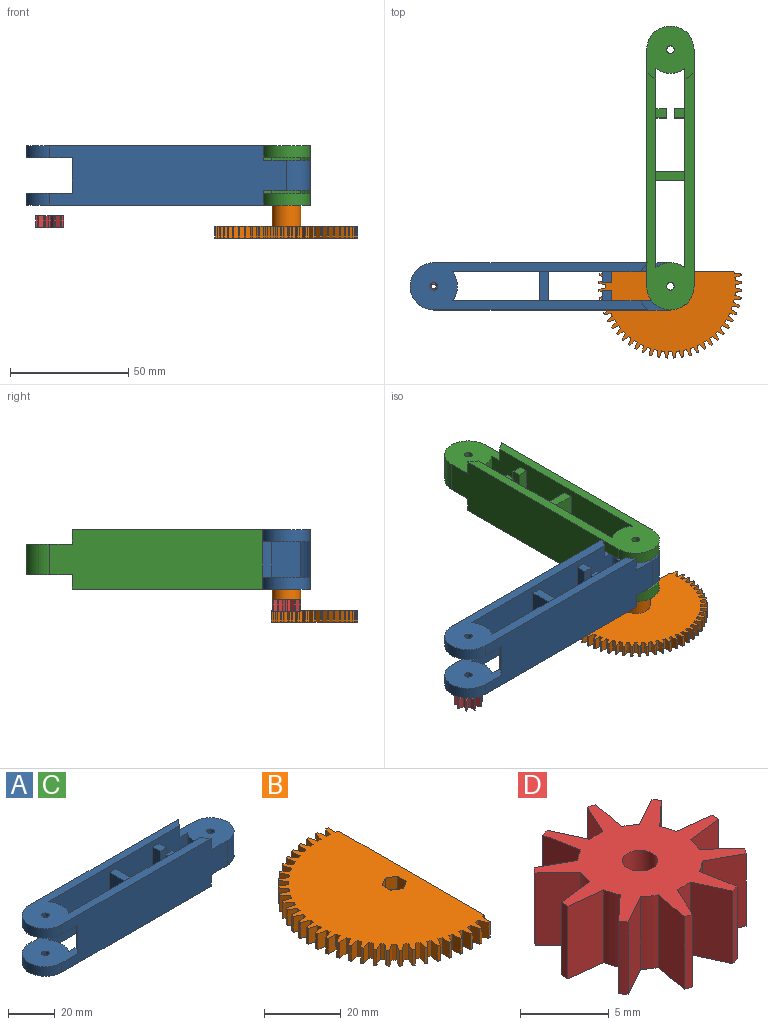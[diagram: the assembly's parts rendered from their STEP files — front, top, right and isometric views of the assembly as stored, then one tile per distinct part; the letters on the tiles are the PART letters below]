
ASSEMBLY  parts=4 mates=3
PART A: 44 faces, bbox 120x20x25 mm
  f0: plane 4.51x3.85mm, normal (0,0,1), area 17.4mm2, adj f1,f2,f5,f42
  f1: plane 19x4.51mm, normal (1,0,0), area 85.7mm2, adj f0,f3,f5,f42
  f2: plane 19x4.51mm, normal (-1,0,0), area 85.7mm2, adj f0,f3,f5,f42
  f3: plane 4.51x3.85mm, normal (0,0,-1), area 17.4mm2, adj f1,f2,f5,f42
  f4: cylinder r=1.6mm len=3.2mm, axis (0,0,-1), area 25.1mm2, adj f36,f41
  f5: plane 84.23x25mm, normal (0,1,0), area 1837.3mm2, adj f0,f1,f2,f3,f9,f11,f14,f15
  f6: plane 100x25mm, normal (0,1,0), area 2241.3mm2, adj f10,f12,f14,f20,f22,f27,f29,f30
  f7: plane 84.23x25mm, normal (0,-1,0), area 1837.3mm2, adj f9,f11,f14,f15,f16,f17,f18,f19
  f8: plane 100x25mm, normal (0,-1,0), area 2241.3mm2, adj f10,f12,f14,f20,f22,f28,f29,f31
  f9: cylinder r=10mm len=12.3mm, axis (0,0,-1), area 66.2mm2, adj f5,f7,f14,f36
  f10: cylinder r=10mm len=20mm, axis (0,0,-1), area 157.1mm2, adj f6,f8,f14,f36
  f11: cylinder r=10mm len=13mm, axis (0,0,-1), area 172.2mm2, adj f5,f7,f29,f32
  f12: cylinder r=10mm len=20mm, axis (0,0,-1), area 408.4mm2, adj f6,f8,f29,f32
  f13: cylinder r=1.6mm len=13mm, axis (0,0,-1), area 130.7mm2, adj f29,f32
  f14: plane 100.42x20mm, normal (0,0,-1), area 905.8mm2, adj f5,f6,f7,f8,f9,f10,f30,f31
  f15: plane 19x12.3mm, normal (-1,0,0), area 233.7mm2, adj f5,f7,f24,f25
  f16: plane 19x4.51mm, normal (1,0,0), area 85.7mm2, adj f7,f23,f26,f43
  f17: plane 19x12.3mm, normal (1,0,0), area 233.7mm2, adj f5,f7,f24,f25
  f18: plane 19x4.51mm, normal (-1,0,0), area 85.7mm2, adj f7,f23,f26,f43
  f19: cylinder r=10mm len=12.3mm, axis (0,0,-1), area 66.2mm2, adj f5,f7,f22,f35
  f20: cylinder r=10mm len=20mm, axis (0,0,-1), area 157.1mm2, adj f6,f8,f22,f35
  f21: cylinder r=1.6mm len=5mm, axis (0,0,-1), area 50.3mm2, adj f22,f35
  f22: plane 100.42x20mm, normal (0,0,1), area 947.8mm2, adj f5,f6,f7,f8,f19,f20,f21,f27
  f23: plane 4.51x3.85mm, normal (0,0,1), area 17.4mm2, adj f7,f16,f18,f43
  f24: plane 12.3x3.85mm, normal (0,0,1), area 47.4mm2, adj f5,f7,f15,f17
  f25: plane 12.3x3.85mm, normal (0,0,-1), area 47.4mm2, adj f5,f7,f15,f17
  f26: plane 4.51x3.85mm, normal (0,0,-1), area 17.4mm2, adj f7,f16,f18,f43
  f27: cylinder r=13.85mm len=6mm, axis (0,0,-1), area 28.8mm2, adj f6,f7,f22,f29
  f28: cylinder r=13.85mm len=6mm, axis (0,0,-1), area 28.8mm2, adj f5,f8,f22,f29
  f29: plane 22.41x20mm, normal (0,0,1), area 349.8mm2, adj f5,f6,f7,f8,f11,f12,f13,f27
  f30: cylinder r=13.85mm len=6mm, axis (0,0,-1), area 28.8mm2, adj f6,f7,f14,f32
  f31: cylinder r=13.85mm len=6mm, axis (0,0,-1), area 28.8mm2, adj f5,f8,f14,f32
  f32: plane 22.41x20mm, normal (0,0,-1), area 349.8mm2, adj f5,f6,f7,f8,f11,f12,f13,f30
  f33: cylinder r=13.85mm len=15mm, axis (0,0,-1), area 72mm2, adj f6,f7,f35,f36
  f34: cylinder r=13.85mm len=15mm, axis (0,0,-1), area 72mm2, adj f5,f8,f35,f36
  f35: plane 22.41x20mm, normal (0,0,-1), area 349.8mm2, adj f5,f6,f7,f8,f19,f20,f21,f33
  f36: plane 22.41x20mm, normal (0,0,1), area 349.8mm2, adj f4,f5,f6,f7,f8,f9,f10,f33
  f37: plane 5x2.5mm, normal (0,1,0), area 12.5mm2, adj f14,f38,f40,f41
  f38: plane 10x2.5mm, normal (-1,0,0), area 25mm2, adj f14,f37,f39,f41
  f39: plane 5x2.5mm, normal (0,-1,0), area 12.5mm2, adj f14,f38,f40,f41
  f40: plane 10x2.5mm, normal (1,0,0), area 25mm2, adj f14,f37,f39,f41
  f41: plane 10x5mm, normal (0,0,-1), area 42mm2, adj f4,f37,f38,f39,f40
  f42: plane 19x3.85mm, normal (0,1,0), area 73.2mm2, adj f0,f1,f2,f3
  f43: plane 19x3.85mm, normal (0,-1,0), area 73.2mm2, adj f16,f18,f23,f26
PART B: 147 faces, bbox 36.6x60.4x15 mm
  f0: cylinder r=1.6mm len=11mm, axis (0,0,-1), area 110.6mm2, adj f39,f146
  f1: plane 60.44x36.63mm, normal (0,0,1), area 1624.9mm2, adj f2,f3,f4,f5,f6,f7,f8,f9
  f2: cylinder r=30.25mm len=5mm, axis (0,0,-1), area 4mm2, adj f1,f34,f75,f136
  f3: cylinder r=30.25mm len=5mm, axis (0,0,-1), area 4mm2, adj f1,f34,f133,f135
  f4: cylinder r=30.25mm len=5mm, axis (0,0,-1), area 4mm2, adj f1,f34,f130,f132
  f5: cylinder r=30.25mm len=5mm, axis (0,0,-1), area 4mm2, adj f1,f34,f127,f129
  f6: cylinder r=30.25mm len=5mm, axis (0,0,-1), area 4mm2, adj f1,f34,f124,f126
  f7: cylinder r=30.25mm len=5mm, axis (0,0,-1), area 4mm2, adj f1,f34,f121,f123
  f8: cylinder r=30.25mm len=5mm, axis (0,0,-1), area 4mm2, adj f1,f34,f114,f118
  f9: cylinder r=30.25mm len=5mm, axis (0,0,-1), area 4mm2, adj f1,f34,f115,f120
  f10: cylinder r=30.25mm len=5mm, axis (0,0,-1), area 4mm2, adj f1,f34,f108,f110
  f11: cylinder r=30.25mm len=5mm, axis (0,0,-1), area 4mm2, adj f1,f34,f105,f109
  f12: cylinder r=30.25mm len=5mm, axis (0,0,-1), area 4mm2, adj f1,f34,f102,f106
  f13: cylinder r=30.25mm len=5mm, axis (0,0,-1), area 4mm2, adj f1,f34,f93,f103
  f14: cylinder r=30.25mm len=5mm, axis (0,0,-1), area 4mm2, adj f1,f34,f96,f100
  f15: cylinder r=30.25mm len=5mm, axis (0,0,-1), area 4mm2, adj f1,f34,f97,f117
  f16: cylinder r=30.25mm len=5mm, axis (0,0,-1), area 4mm2, adj f1,f34,f90,f94
  f17: cylinder r=30.25mm len=5mm, axis (0,0,-1), area 4mm2, adj f1,f34,f91,f99
  f18: cylinder r=30.25mm len=5mm, axis (0,0,-1), area 4mm2, adj f1,f34,f78,f88
  f19: cylinder r=30.25mm len=5mm, axis (0,0,-1), area 4mm2, adj f1,f34,f85,f87
  f20: cylinder r=30.25mm len=5mm, axis (0,0,-1), area 4mm2, adj f1,f34,f63,f82
  f21: cylinder r=30.25mm len=5mm, axis (0,0,-1), area 4mm2, adj f1,f34,f79,f81
  f22: cylinder r=30.25mm len=5mm, axis (0,0,-1), area 4mm2, adj f1,f34,f72,f76
  f23: cylinder r=30.25mm len=5mm, axis (0,0,-1), area 4mm2, adj f1,f34,f66,f73
  f24: cylinder r=30.25mm len=5mm, axis (0,0,-1), area 4mm2, adj f1,f34,f70,f84
  f25: cylinder r=30.25mm len=5mm, axis (0,0,-1), area 4mm2, adj f1,f34,f67,f69
  f26: cylinder r=30.25mm len=5mm, axis (0,0,-1), area 4mm2, adj f1,f34,f60,f64
  f27: cylinder r=30.25mm len=5mm, axis (0,0,-1), area 4mm2, adj f1,f34,f57,f61
  f28: cylinder r=30.25mm len=5mm, axis (0,0,-1), area 4mm2, adj f1,f34,f54,f58
  f29: cylinder r=30.25mm len=5mm, axis (0,0,-1), area 4mm2, adj f1,f34,f51,f55
  f30: cylinder r=30.25mm len=5mm, axis (0,0,-1), area 4mm2, adj f1,f34,f49,f52
  f31: cylinder r=30.25mm len=5mm, axis (0,0,-1), area 4mm2, adj f1,f34,f44,f47
  f32: cylinder r=30.25mm len=5mm, axis (0,0,-1), area 4mm2, adj f1,f34,f41,f45
  f33: cylinder r=30.25mm len=5mm, axis (0,0,-1), area 4mm2, adj f1,f34,f42,f112
  f34: plane 60.44x36.63mm, normal (0,0,-1), area 1538.5mm2, adj f2,f3,f4,f5,f6,f7,f8,f9
  f35: plane 9.5x1mm, normal (1,0,0), area 9.5mm2, adj f36,f38,f39,f139
  f36: plane 4.5x1mm, normal (0,1,0), area 4.5mm2, adj f35,f37,f39,f139
  f37: plane 9.5x1mm, normal (-1,0,0), area 9.5mm2, adj f36,f38,f39,f139
  f38: plane 4.5x1mm, normal (0,-1,0), area 4.5mm2, adj f35,f37,f39,f139
  f39: plane 9.5x4.5mm, normal (0,0,-1), area 34.7mm2, adj f0,f35,f36,f37,f38
  f40: cylinder r=27.5mm len=5mm, axis (0,0,-1), area 6.2mm2, adj f1,f34,f41,f42
  f41: plane 5x2.73mm, normal (-0.97,-0.24,0), area 14.1mm2, adj f1,f32,f34,f40
  f42: plane 5x2.73mm, normal (0.97,-0.24,0), area 14.1mm2, adj f1,f33,f34,f40
  f43: cylinder r=27.5mm len=5mm, axis (0,0,-1), area 6.2mm2, adj f1,f34,f44,f45
  f44: plane 5x2.64mm, normal (-0.94,-0.35,0), area 14.1mm2, adj f1,f31,f34,f43
  f45: plane 5x2.79mm, normal (0.99,-0.13,0), area 14.1mm2, adj f1,f32,f34,f43
  f46: cylinder r=27.5mm len=5mm, axis (0,0,-1), area 4.6mm2, adj f1,f34,f47,f137
  f47: plane 5x2.81mm, normal (1,-0.02,0), area 14.1mm2, adj f1,f31,f34,f46
  f48: cylinder r=27.5mm len=5mm, axis (0,0,-1), area 4.6mm2, adj f1,f34,f49,f137
  f49: plane 5x2.81mm, normal (1,0.02,0), area 14.1mm2, adj f1,f30,f34,f48
  f50: cylinder r=27.5mm len=5mm, axis (0,0,-1), area 6.2mm2, adj f1,f34,f51,f52
  f51: plane 5x2.79mm, normal (0.99,0.13,0), area 14.1mm2, adj f1,f29,f34,f50
  f52: plane 5x2.64mm, normal (-0.94,0.35,0), area 14.1mm2, adj f1,f30,f34,f50
  f53: cylinder r=27.5mm len=5mm, axis (0,0,-1), area 6.2mm2, adj f1,f34,f54,f55
  f54: plane 5x2.73mm, normal (0.97,0.24,0), area 14.1mm2, adj f1,f28,f34,f53
  f55: plane 5x2.73mm, normal (-0.97,0.24,0), area 14.1mm2, adj f1,f29,f34,f53
  f56: cylinder r=27.5mm len=5mm, axis (0,0,-1), area 6.2mm2, adj f1,f34,f57,f58
  f57: plane 5x2.64mm, normal (0.94,0.35,0), area 14.1mm2, adj f1,f27,f34,f56
  f58: plane 5x2.79mm, normal (-0.99,0.13,0), area 14.1mm2, adj f1,f28,f34,f56
  f59: cylinder r=27.5mm len=5mm, axis (0,0,-1), area 6.2mm2, adj f1,f34,f60,f61
  f60: plane 5x2.51mm, normal (0.89,0.45,0), area 14.1mm2, adj f1,f26,f34,f59
  f61: plane 5x2.81mm, normal (-1,0.02,0), area 14.1mm2, adj f1,f27,f34,f59
  f62: cylinder r=27.5mm len=5mm, axis (0,0,-1), area 6.2mm2, adj f1,f34,f63,f64
  f63: plane 5x2.35mm, normal (0.84,0.55,0), area 14.1mm2, adj f1,f20,f34,f62
  f64: plane 5x2.8mm, normal (-1,-0.09,0), area 14.1mm2, adj f1,f26,f34,f62
  f65: cylinder r=27.5mm len=5mm, axis (0,0,-1), area 6.2mm2, adj f1,f34,f66,f67
  f66: plane 5x2.67mm, normal (0.31,0.95,0), area 14.1mm2, adj f1,f23,f34,f65
  f67: plane 5x2.03mm, normal (-0.72,-0.69,0), area 14.1mm2, adj f1,f25,f34,f65
  f68: cylinder r=27.5mm len=5mm, axis (0,0,-1), area 6.2mm2, adj f1,f34,f69,f70
  f69: plane 5x2.56mm, normal (0.42,0.91,0), area 14.1mm2, adj f1,f25,f34,f68
  f70: plane 5x2.23mm, normal (-0.79,-0.61,0), area 14.1mm2, adj f1,f24,f34,f68
  f71: cylinder r=27.5mm len=5mm, axis (0,0,-1), area 6.2mm2, adj f1,f34,f72,f73
  f72: plane 5x2.75mm, normal (0.2,0.98,0), area 14.1mm2, adj f1,f22,f34,f71
  f73: plane 5x2.16mm, normal (-0.64,-0.77,0), area 14.1mm2, adj f1,f23,f34,f71
  f74: cylinder r=27.5mm len=5mm, axis (0,0,-1), area 6.2mm2, adj f1,f34,f75,f76
  f75: plane 5x2.8mm, normal (0.09,1,0), area 14.1mm2, adj f1,f2,f34,f74
  f76: plane 5x2.35mm, normal (-0.55,-0.84,0), area 14.1mm2, adj f1,f22,f34,f74
  f77: cylinder r=27.5mm len=5mm, axis (0,0,-1), area 6.2mm2, adj f1,f34,f78,f79
  f78: plane 5x2.03mm, normal (0.69,0.72,0), area 14.1mm2, adj f1,f18,f34,f77
  f79: plane 5x2.67mm, normal (-0.95,-0.31,0), area 14.1mm2, adj f1,f21,f34,f77
  f80: cylinder r=27.5mm len=5mm, axis (0,0,-1), area 6.2mm2, adj f1,f34,f81,f82
  f81: plane 5x2.16mm, normal (0.77,0.64,0), area 14.1mm2, adj f1,f21,f34,f80
  f82: plane 5x2.75mm, normal (-0.98,-0.2,0), area 14.1mm2, adj f1,f20,f34,f80
  f83: cylinder r=27.5mm len=5mm, axis (0,0,-1), area 6.2mm2, adj f1,f34,f84,f85
  f84: plane 5x2.41mm, normal (0.52,0.86,0), area 14.1mm2, adj f1,f24,f34,f83
  f85: plane 5x2.41mm, normal (-0.86,-0.52,0), area 14.1mm2, adj f1,f19,f34,f83
  f86: cylinder r=27.5mm len=5mm, axis (0,0,-1), area 6.2mm2, adj f1,f34,f87,f88
  f87: plane 5x2.23mm, normal (0.61,0.79,0), area 14.1mm2, adj f1,f19,f34,f86
  f88: plane 5x2.56mm, normal (-0.91,-0.42,0), area 14.1mm2, adj f1,f18,f34,f86
  f89: cylinder r=27.5mm len=5mm, axis (0,0,-1), area 6.2mm2, adj f1,f34,f90,f91
  f90: plane 5x2.56mm, normal (-0.91,0.42,0), area 14.1mm2, adj f1,f16,f34,f89
  f91: plane 5x2.23mm, normal (0.61,-0.79,0), area 14.1mm2, adj f1,f17,f34,f89
  f92: cylinder r=27.5mm len=5mm, axis (0,0,-1), area 6.2mm2, adj f1,f34,f93,f94
  f93: plane 5x2.67mm, normal (-0.95,0.31,0), area 14.1mm2, adj f1,f13,f34,f92
  f94: plane 5x2.03mm, normal (0.69,-0.72,0), area 14.1mm2, adj f1,f16,f34,f92
  f95: cylinder r=27.5mm len=5mm, axis (0,0,-1), area 6.2mm2, adj f1,f34,f96,f97
  f96: plane 5x2.23mm, normal (-0.79,0.61,0), area 14.1mm2, adj f1,f14,f34,f95
  f97: plane 5x2.56mm, normal (0.42,-0.91,0), area 14.1mm2, adj f1,f15,f34,f95
  f98: cylinder r=27.5mm len=5mm, axis (0,0,-1), area 6.2mm2, adj f1,f34,f99,f100
  f99: plane 5x2.41mm, normal (-0.86,0.52,0), area 14.1mm2, adj f1,f17,f34,f98
  f100: plane 5x2.41mm, normal (0.52,-0.86,0), area 14.1mm2, adj f1,f14,f34,f98
  f101: cylinder r=27.5mm len=5mm, axis (0,0,-1), area 6.2mm2, adj f1,f34,f102,f103
  f102: plane 5x2.75mm, normal (-0.98,0.2,0), area 14.1mm2, adj f1,f12,f34,f101
  f103: plane 5x2.16mm, normal (0.77,-0.64,0), area 14.1mm2, adj f1,f13,f34,f101
  f104: cylinder r=27.5mm len=5mm, axis (0,0,-1), area 6.2mm2, adj f1,f34,f105,f106
  f105: plane 5x2.8mm, normal (-1,0.09,0), area 14.1mm2, adj f1,f11,f34,f104
  f106: plane 5x2.35mm, normal (0.84,-0.55,0), area 14.1mm2, adj f1,f12,f34,f104
  f107: cylinder r=27.5mm len=5mm, axis (0,0,-1), area 6.2mm2, adj f1,f34,f108,f109
  f108: plane 5x2.81mm, normal (-1,-0.02,0), area 14.1mm2, adj f1,f10,f34,f107
  f109: plane 5x2.51mm, normal (0.89,-0.45,0), area 14.1mm2, adj f1,f11,f34,f107
  f110: plane 5x2.64mm, normal (0.94,-0.35,0), area 14.1mm2, adj f1,f10,f34,f111
  f111: cylinder r=27.5mm len=5mm, axis (0,0,-1), area 6.2mm2, adj f1,f34,f110,f112
  f112: plane 5x2.79mm, normal (-0.99,-0.13,0), area 14.1mm2, adj f1,f33,f34,f111
  f113: cylinder r=27.5mm len=5mm, axis (0,0,-1), area 6.2mm2, adj f1,f34,f114,f115
  f114: plane 5x2.16mm, normal (-0.64,0.77,0), area 14.1mm2, adj f1,f8,f34,f113
  f115: plane 5x2.75mm, normal (0.2,-0.98,0), area 14.1mm2, adj f1,f9,f34,f113
  f116: cylinder r=27.5mm len=5mm, axis (0,0,-1), area 6.2mm2, adj f1,f34,f117,f118
  f117: plane 5x2.03mm, normal (-0.72,0.69,0), area 14.1mm2, adj f1,f15,f34,f116
  f118: plane 5x2.67mm, normal (0.31,-0.95,0), area 14.1mm2, adj f1,f8,f34,f116
  f119: cylinder r=27.5mm len=5mm, axis (0,0,-1), area 6.2mm2, adj f1,f34,f120,f121
  f120: plane 5x2.35mm, normal (-0.55,0.84,0), area 14.1mm2, adj f1,f9,f34,f119
  f121: plane 5x2.8mm, normal (0.09,-1,0), area 14.1mm2, adj f1,f7,f34,f119
  f122: cylinder r=27.5mm len=5mm, axis (0,0,-1), area 6.2mm2, adj f1,f34,f123,f124
  f123: plane 5x2.51mm, normal (-0.45,0.89,0), area 14.1mm2, adj f1,f7,f34,f122
  f124: plane 5x2.81mm, normal (-0.02,-1,0), area 14.1mm2, adj f1,f6,f34,f122
  f125: cylinder r=27.5mm len=5mm, axis (0,0,-1), area 6.2mm2, adj f1,f34,f126,f127
  f126: plane 5x2.64mm, normal (-0.35,0.94,0), area 14.1mm2, adj f1,f6,f34,f125
  f127: plane 5x2.79mm, normal (-0.13,-0.99,0), area 14.1mm2, adj f1,f5,f34,f125
  f128: cylinder r=27.5mm len=5mm, axis (0,0,-1), area 6.2mm2, adj f1,f34,f129,f130
  f129: plane 5x2.73mm, normal (-0.24,0.97,0), area 14.1mm2, adj f1,f5,f34,f128
  f130: plane 5x2.73mm, normal (-0.24,-0.97,0), area 14.1mm2, adj f1,f4,f34,f128
  f131: cylinder r=27.5mm len=5mm, axis (0,0,-1), area 6.2mm2, adj f1,f34,f132,f133
  f132: plane 5x2.79mm, normal (-0.13,0.99,0), area 14.1mm2, adj f1,f4,f34,f131
  f133: plane 5x2.64mm, normal (-0.35,-0.94,0), area 14.1mm2, adj f1,f3,f34,f131
  f134: cylinder r=27.5mm len=5mm, axis (0,0,-1), area 6.2mm2, adj f1,f34,f135,f136
  f135: plane 5x2.81mm, normal (-0.02,1,0), area 14.1mm2, adj f1,f3,f34,f134
  f136: plane 5x2.51mm, normal (-0.45,-0.89,0), area 14.1mm2, adj f1,f2,f34,f134
  f137: plane 53.49x5mm, normal (1,0,0), area 267.4mm2, adj f1,f34,f46,f48
  f138: cylinder r=6.04mm len=12.08mm, axis (0,0,1), area 341.5mm2, adj f34,f139
  f139: plane 12.08x12.08mm, normal (0,0,-1), area 71.8mm2, adj f35,f36,f37,f38,f138
  f140: plane 4x2.85mm, normal (-0.5,-0.87,0), area 13.2mm2, adj f1,f141,f145,f146
  f141: plane 4x2.85mm, normal (0.5,-0.87,0), area 13.2mm2, adj f1,f140,f142,f146
  f142: plane 4x3.29mm, normal (1,0,0), area 13.2mm2, adj f1,f141,f143,f146
  f143: plane 4x2.85mm, normal (0.5,0.87,0), area 13.2mm2, adj f1,f142,f144,f146
  f144: plane 4x2.85mm, normal (-0.5,0.87,0), area 13.2mm2, adj f1,f143,f145,f146
  f145: plane 4x3.29mm, normal (-1,0,0), area 13.2mm2, adj f1,f140,f144,f146
  f146: plane 6.58x5.7mm, normal (0,0,1), area 20.1mm2, adj f0,f140,f141,f142,f143,f144,f145
PART C: same geometry as A
PART D: 45 faces, bbox 12x11.6x5 mm
  f0: cylinder r=6mm len=5mm, axis (0,0,-1), area 2.7mm2, adj f9,f10,f34,f41
  f1: cylinder r=6mm len=5mm, axis (0,0,-1), area 2.7mm2, adj f9,f10,f38,f40
  f2: cylinder r=6mm len=5mm, axis (0,0,-1), area 2.7mm2, adj f9,f10,f31,f35
  f3: cylinder r=6mm len=5mm, axis (0,0,-1), area 2.7mm2, adj f9,f10,f16,f32
  f4: cylinder r=6mm len=5mm, axis (0,0,-1), area 2.7mm2, adj f9,f10,f25,f29
  f5: cylinder r=6mm len=5mm, axis (0,0,-1), area 2.7mm2, adj f9,f10,f26,f37
  f6: cylinder r=6mm len=5mm, axis (0,0,-1), area 2.7mm2, adj f9,f10,f19,f21
  f7: cylinder r=6mm len=5mm, axis (0,0,-1), area 2.7mm2, adj f9,f10,f20,f28
  f8: cylinder r=6mm len=5mm, axis (0,0,-1), area 2.7mm2, adj f9,f10,f13,f17
  f9: plane 12x11.57mm, normal (0,0,1), area 56.5mm2, adj f0,f1,f2,f3,f4,f5,f6,f7
  f10: plane 12x11.57mm, normal (0,0,-1), area 42.3mm2, adj f0,f1,f2,f3,f4,f5,f6,f7
  f11: cylinder r=6mm len=5mm, axis (0,0,-1), area 2.7mm2, adj f9,f10,f14,f23
  f12: cylinder r=3.5mm len=5mm, axis (0,0,-1), area 5.2mm2, adj f9,f10,f13,f14
  f13: plane 5x2.32mm, normal (-0.91,-0.42,0), area 12.8mm2, adj f8,f9,f10,f12
  f14: plane 5x2.32mm, normal (0.91,-0.42,0), area 12.8mm2, adj f9,f10,f11,f12
  f15: cylinder r=3.5mm len=5mm, axis (0,0,-1), area 5.2mm2, adj f9,f10,f16,f17
  f16: plane 5x2.24mm, normal (-0.48,-0.87,0), area 12.8mm2, adj f3,f9,f10,f15
  f17: plane 5x2.51mm, normal (0.98,0.19,0), area 12.8mm2, adj f8,f9,f10,f15
  f18: cylinder r=3.5mm len=5mm, axis (0,0,-1), area 5.2mm2, adj f9,f10,f19,f20
  f19: plane 5x1.87mm, normal (-0.68,0.73,0), area 12.8mm2, adj f6,f9,f10,f18
  f20: plane 5x2.54mm, normal (-0.12,-0.99,0), area 12.8mm2, adj f7,f9,f10,f18
  f21: plane 5x2.24mm, normal (0.48,-0.87,0), area 12.8mm2, adj f6,f9,f10,f22
  f22: cylinder r=3.5mm len=5mm, axis (0,0,-1), area 5.2mm2, adj f9,f10,f21,f23
  f23: plane 5x2.51mm, normal (-0.98,0.19,0), area 12.8mm2, adj f9,f10,f11,f22
  f24: cylinder r=3.5mm len=5mm, axis (0,0,-1), area 5.2mm2, adj f9,f10,f25,f26
  f25: plane 5x2.24mm, normal (0.48,0.87,0), area 12.8mm2, adj f4,f9,f10,f24
  f26: plane 5x2.51mm, normal (-0.98,-0.19,0), area 12.8mm2, adj f5,f9,f10,f24
  f27: cylinder r=3.5mm len=5mm, axis (0,0,-1), area 5.2mm2, adj f9,f10,f28,f29
  f28: plane 5x2.54mm, normal (-0.12,0.99,0), area 12.8mm2, adj f7,f9,f10,f27
  f29: plane 5x1.87mm, normal (-0.68,-0.73,0), area 12.8mm2, adj f4,f9,f10,f27
  f30: cylinder r=3.5mm len=5mm, axis (0,0,-1), area 5.2mm2, adj f9,f10,f31,f32
  f31: plane 5x2.54mm, normal (0.12,-0.99,0), area 12.8mm2, adj f2,f9,f10,f30
  f32: plane 5x1.87mm, normal (0.68,0.73,0), area 12.8mm2, adj f3,f9,f10,f30
  f33: cylinder r=3.5mm len=5mm, axis (0,0,-1), area 5.2mm2, adj f9,f10,f34,f35
  f34: plane 5x1.87mm, normal (0.68,-0.73,0), area 12.8mm2, adj f0,f9,f10,f33
  f35: plane 5x2.54mm, normal (0.12,0.99,0), area 12.8mm2, adj f2,f9,f10,f33
  f36: cylinder r=3.5mm len=5mm, axis (0,0,-1), area 5.2mm2, adj f9,f10,f37,f38
  f37: plane 5x2.32mm, normal (0.91,0.42,0), area 12.8mm2, adj f5,f9,f10,f36
  f38: plane 5x2.32mm, normal (-0.91,0.42,0), area 12.8mm2, adj f1,f9,f10,f36
  f39: cylinder r=3.5mm len=5mm, axis (0,0,-1), area 5.2mm2, adj f9,f10,f40,f41
  f40: plane 5x2.51mm, normal (0.98,-0.19,0), area 12.8mm2, adj f1,f9,f10,f39
  f41: plane 5x2.24mm, normal (-0.48,0.87,0), area 12.8mm2, adj f0,f9,f10,f39
  f42: cylinder r=2.35mm len=4.7mm, axis (0,0,-1), area 44.3mm2, adj f10,f43
  f43: plane 4.7x4.7mm, normal (0,0,-1), area 14.2mm2, adj f42,f44
  f44: cylinder r=1mm len=2mm, axis (0,0,-1), area 12.6mm2, adj f9,f43
PLACE A t=(-73.15,33.91,-14.58)mm fixed
PLACE B rot(axis=(-0.71,-0.71,0),180deg) t=(-59.58,64.82,-23.58)mm
PLACE C rot(axis=(0,0,1),90deg) t=(-28.66,151.25,-14.58)mm
PLACE D rot(axis=(0,0,1),36deg) t=(-159.58,64.82,-24.08)mm
MATE revolute A.f11 <-> C.f4  axis (0,0,1) through (-59.58,64.82,4.42)mm
MATE fastened B.f0 <-> C.f4  axis (0,0,1) through (-59.58,64.82,-13.58)mm
MATE revolute D.f0 <-> A.f4  axis (0,0,1) through (-159.58,64.82,-19.08)mm
